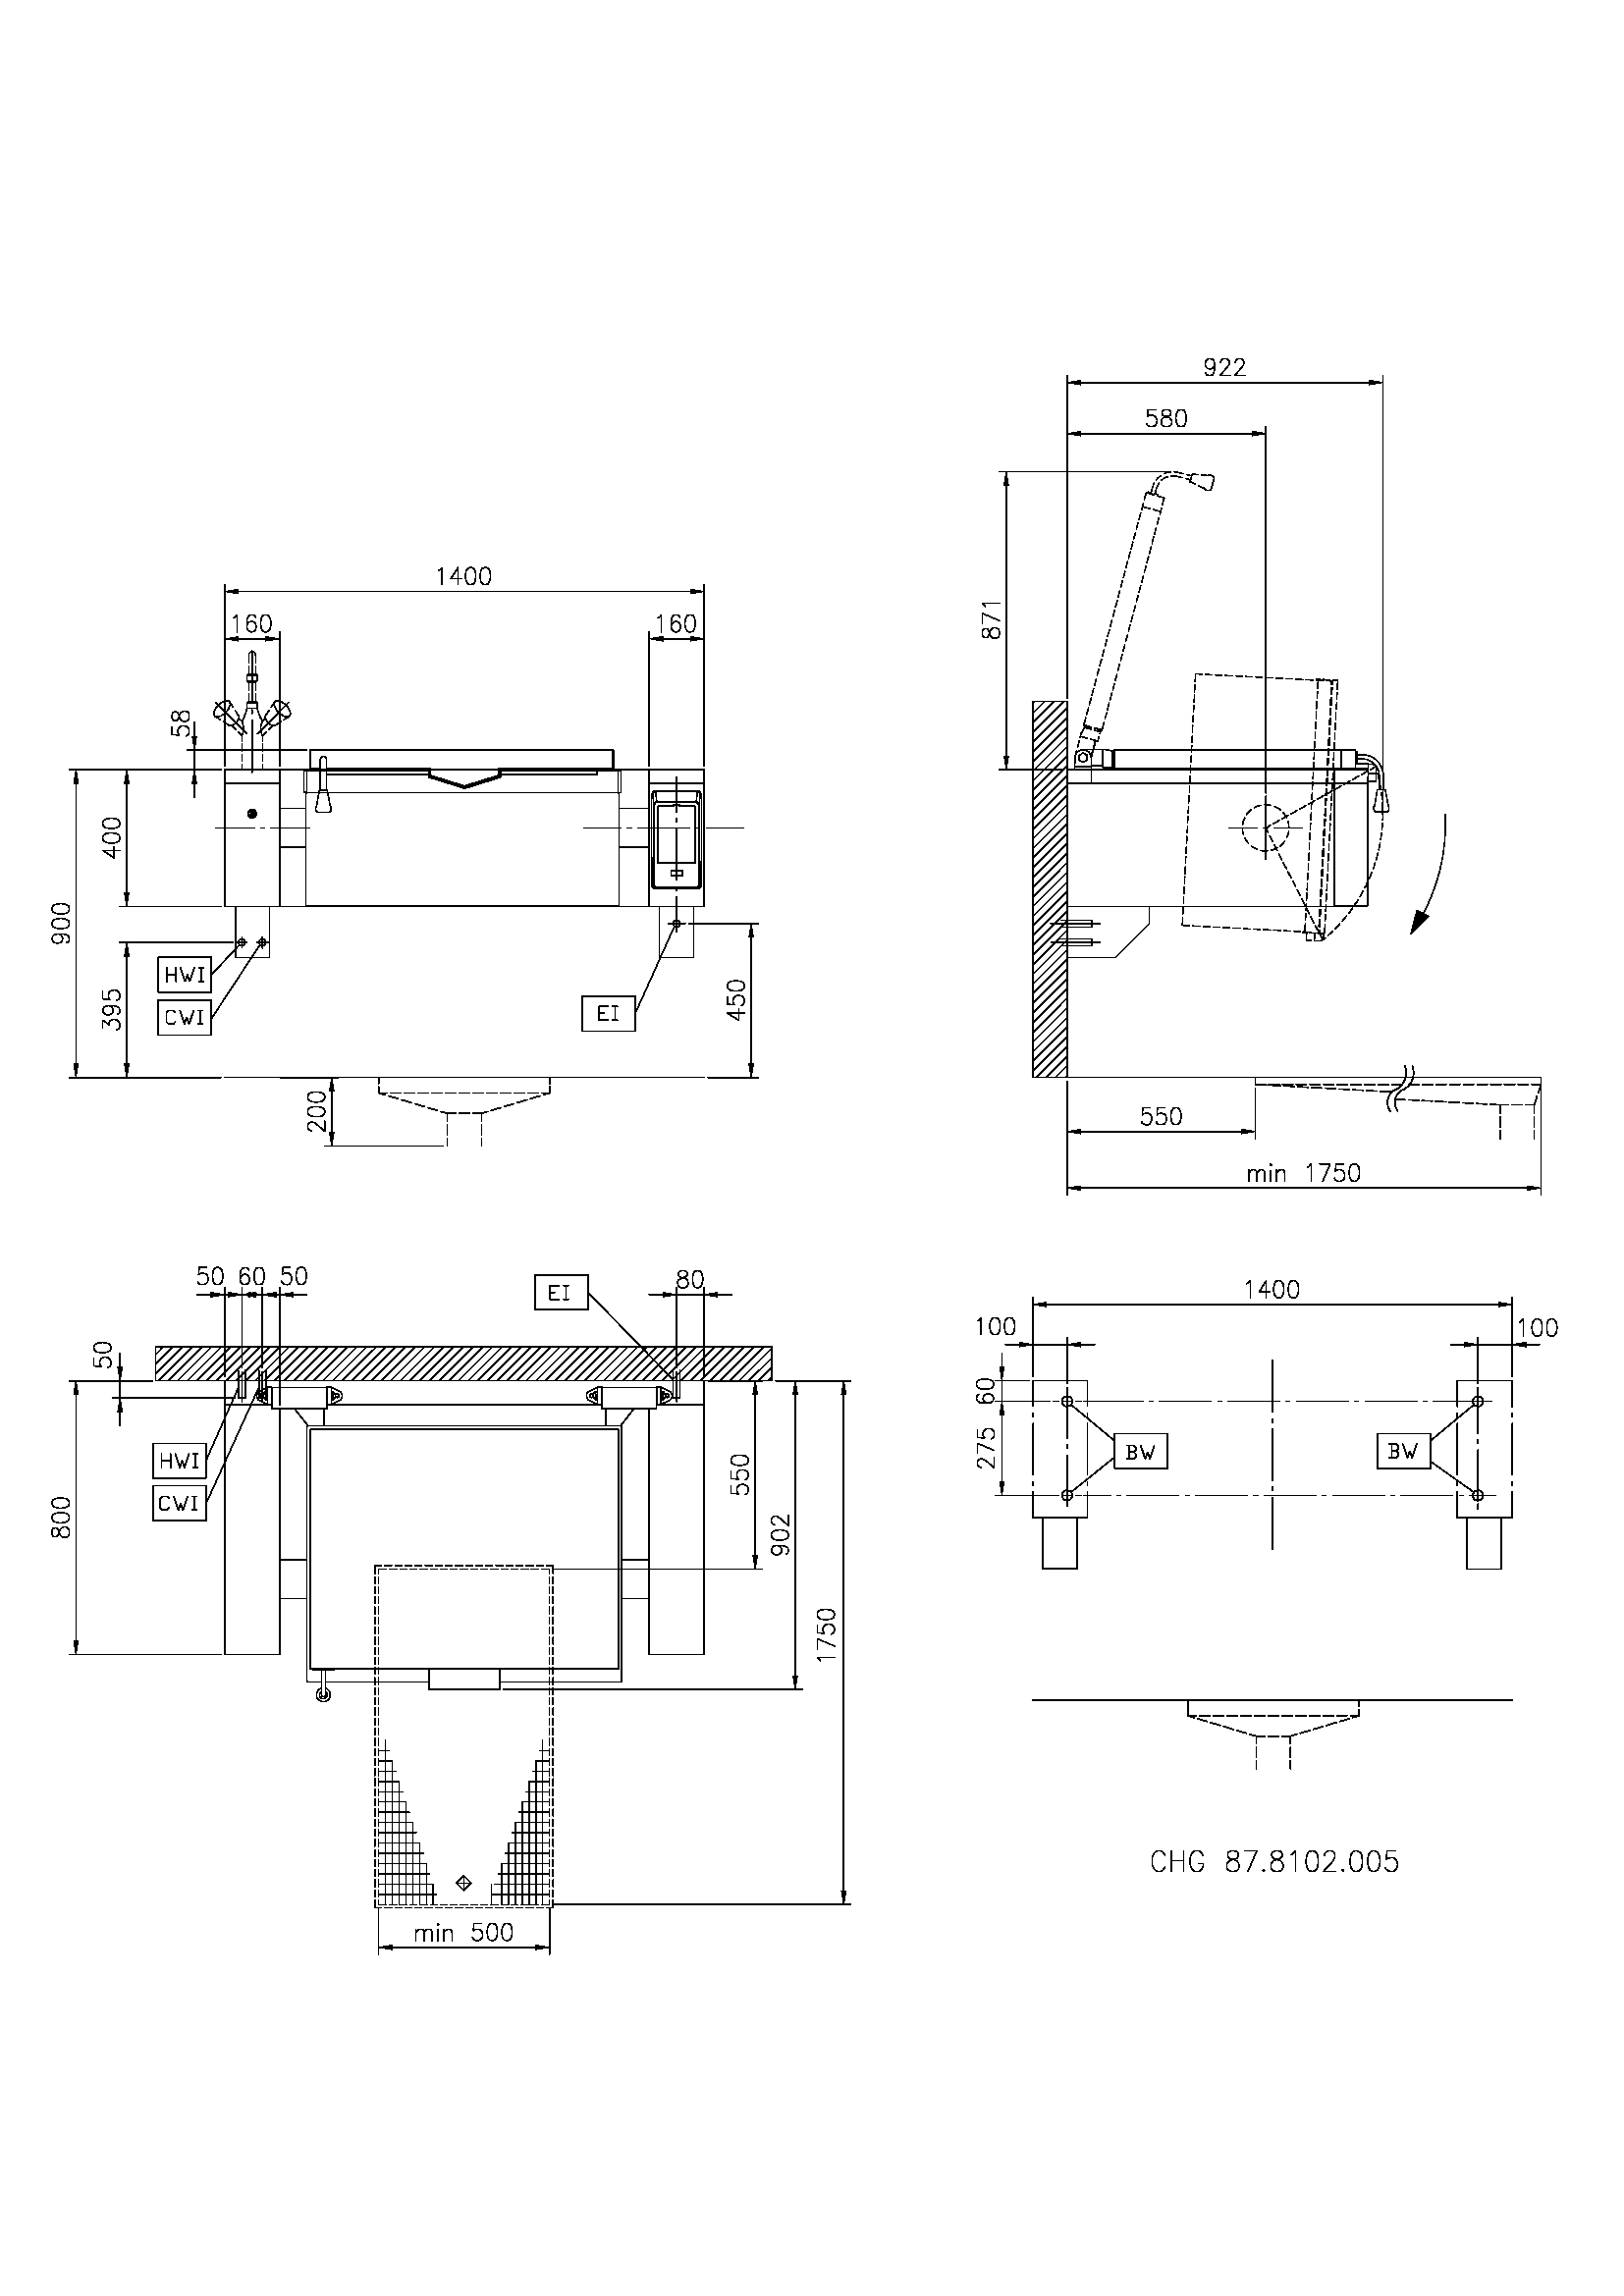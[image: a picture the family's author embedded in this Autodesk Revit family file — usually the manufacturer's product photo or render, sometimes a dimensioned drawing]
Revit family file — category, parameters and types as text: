
# Revit family: QF_ELECTROLUXPROFESSIONAL_586284_PFET08EBEO
name_source: partatom
category: Attrezzature speciali
units: mm (PartAtom-declared; Revit-internal decimal feet)

## family parameters
Basato su piano di lavoro = No
Condiviso = No
Punto di calcolo locali = No
Quota connettore circolare = Usa diametro
Sempre verticale = Sì
Taglio con vuoti quando caricato = No
Tipo di parte = Normale

## types (1)
- Standard
    Accessory = Sì
    Cold Water Size = 13 mm
    Compressed Air Pressure = 0.0 Pa
    Compressed Air Size = 0 mm
    Compressed Air Volume = 0.0 L/s
    Condensate Return Size = 0 mm
    Cycle = 50 Hz
    Depth Actual = 850 mm  [stored 2.78871 ft]
    Descrizione = ELECTRIC TILTING BRAISING PAN, 80L, COMPOUND(H) FS D850
    Direct Waste Size = 0 mm
    Gas Input Pressure = 0
    Gas KW = 0
    Gas Size = 0 mm
    HP = 27.6 HP
    Height Actual = 700 mm  [stored 2.29659 ft]
    Hot Water Size = 13 mm
    Item Number = 586284
    Length Actual = 1400 mm  [stored 4.59318 ft]
    Modello = PFET08EBEO
    Phase = 3
    Produttore = Electrolux Professional
    Prospetto di default = 0 mm  [stored 0 ft]
    Refrigerant Compressor Remote = Sì
    Refrigeration Liquid Line Size = 0 mm  [stored 0 ft]
    Refrigeration Suction Line Size = 0 mm  [stored 0 ft]
    Steam Consumption per Hour = 0
    Steam Supply Maximum Pressure = 0.0 Pa
    Steam Supply Minimum Pressure = 0.0 Pa
    Steam Supply Size = 0 mm
    URL = https://www.electroluxprofessional.com
    URL Manufacturer = https://www.electroluxprofessional.com
    Volts = 400 V
    Watts = 20600 W
    Weight = 240.00 kg

note: source unit labels omitted for Gas Input Pressure — the stored unit's dimension contradicts the parameter name (converter mislabeling)

note: [stored X ft] marks values corroborated as IEEE doubles in the binary element streams (Revit-internal decimal feet)

## geometry (parser evidence)
native form markers: Blend x10, Sweep x7
no freeform markers — native parametric forms only
